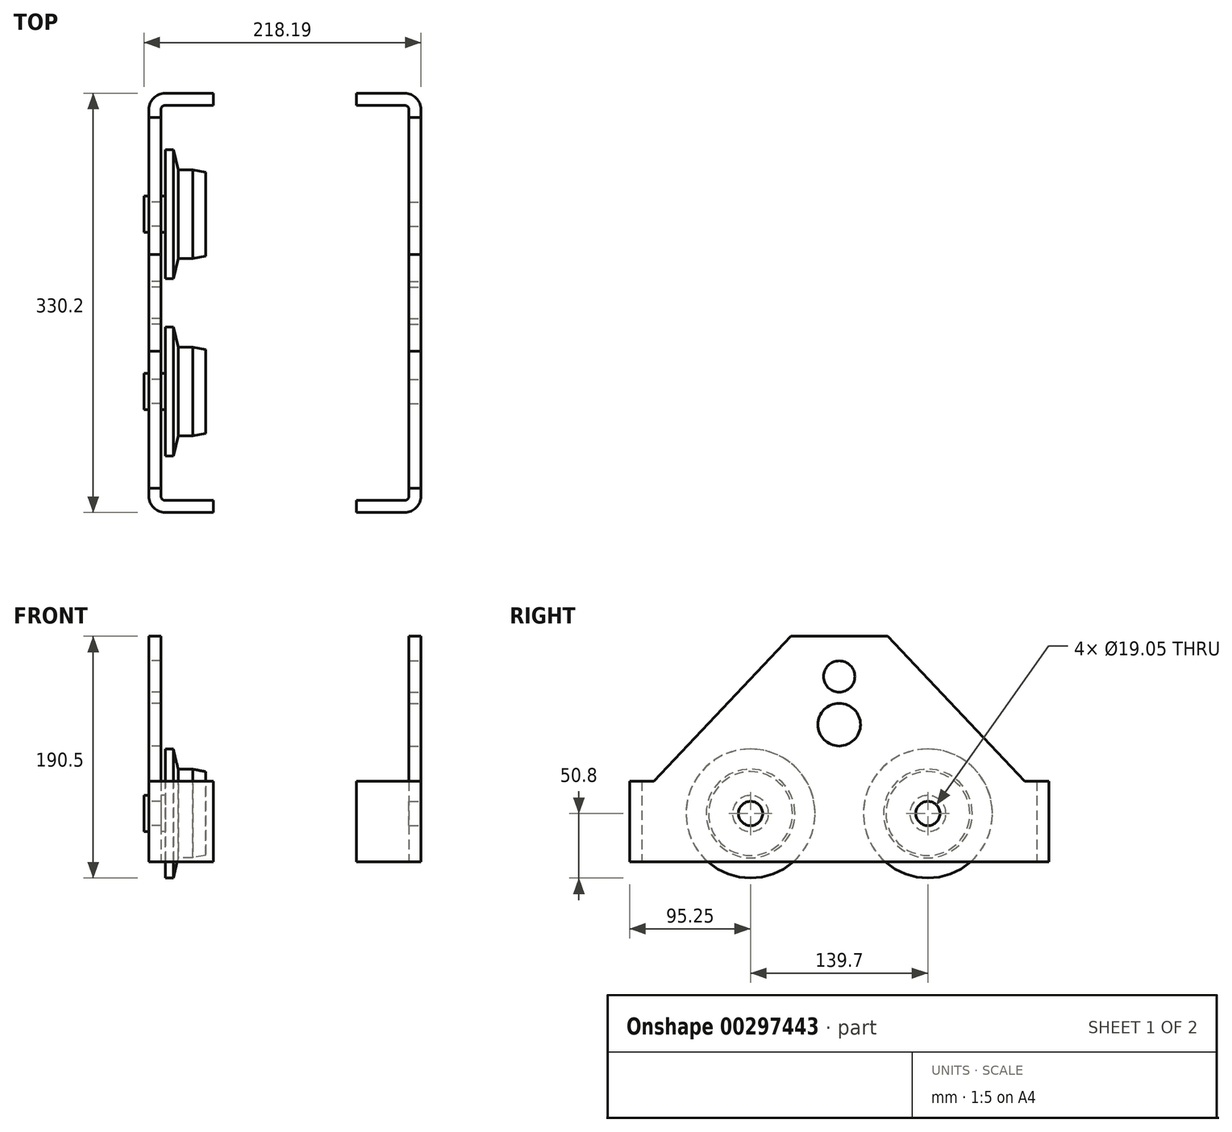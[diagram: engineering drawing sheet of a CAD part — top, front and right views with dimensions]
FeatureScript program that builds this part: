
annotation { "Feature Type Name" : "Feature", "Feature Type Description" : "" }
export const myFeature = defineFeature(function(context is Context, id is Id, definition is map)
    precondition{}
    {
        {
            var Q0;
            Q0=qCreatedBy(makeId("Top.planeOp"),FACE);
            var sketch = newSketch(context, id + "F0", { "sketchPlane" : qUnion([Q0])});
            skLineSegment(sketch, "E0", {"start": v(0, 0) * mm, "end": v(41.32, 0) * mm, "construction": true});
            skLineSegment(sketch, "E1", {"start": v(0, 0) * mm, "end": v(0, 152.4) * mm});
            skLineSegment(sketch, "E2", {"start": v(12.7, 165.1) * mm, "end": v(50.8, 165.1) * mm});
            skPoint(sketch, "E3.visualSharp", {"position": v(0, 165.1) * mm});
            skArc(sketch, "E3.filletArc", {"start": v(12.7, 165.1) * mm, "mid": v(3.72, 161.38) * mm, "end": v(0, 152.4) * mm});
            skLineSegment(sketch, "E4.MirrorCS", {"start": v(12.7, -165.1) * mm, "end": v(50.8, -165.1) * mm});
            skLineSegment(sketch, "E5.MirrorCS", {"start": v(0, 0) * mm, "end": v(0, -152.4) * mm});
            skArc(sketch, "E6.MirrorCS", {"start": v(12.7, -165.1) * mm, "mid": v(3.72, -161.38) * mm, "end": v(0, -152.4) * mm});
            skPoint(sketch, "E7.MirrorP", {"position": v(0, -165.1) * mm});
            skLineSegment(sketch, "E8.0", {"start": v(12.7, -155.58) * mm, "end": v(50.8, -155.58) * mm});
            skArc(sketch, "E8.1", {"start": v(12.7, -155.58) * mm, "mid": v(10.45, -154.65) * mm, "end": v(9.53, -152.4) * mm});
            skLineSegment(sketch, "E8.2", {"start": v(12.7, 155.58) * mm, "end": v(50.8, 155.58) * mm});
            skArc(sketch, "E8.3", {"start": v(12.7, 155.58) * mm, "mid": v(10.45, 154.65) * mm, "end": v(9.53, 152.4) * mm});
            skLineSegment(sketch, "E8.4", {"start": v(9.53, 0) * mm, "end": v(9.53, 152.4) * mm});
            skLineSegment(sketch, "E8.5", {"start": v(9.53, 0) * mm, "end": v(9.53, -152.4) * mm});
            skLineSegment(sketch, "E9", {"start": v(50.8, 165.1) * mm, "end": v(50.8, 155.58) * mm});
            skLineSegment(sketch, "E10", {"start": v(50.8, -155.58) * mm, "end": v(50.8, -165.1) * mm});
            skSolve(sketch);
        }
        {
            var Q0;
            Q0 = qSketchRegion(id + "F0", true);
            extrude(context, id + "F1", {"entities" : qUnion([Q0]), "depth" : 177.8 * mm});
        }
        {
            var Q0;
            Q0=makeQuery(id+"F1.opExtrude","SWEPT_FACE",FACE,{"disambiguationData":[OSD([sQuery(id+"F0.wireOp",EDGE,"E1"),sQuery(id+"F0.wireOp",EDGE,"E5.MirrorCS")])]});
            var sketch = newSketch(context, id + "F2", { "sketchPlane" : qUnion([Q0])});
            skLineSegment(sketch, "E11", {"start": v(-165.1, 63.5) * mm, "end": v(-146.05, 63.5) * mm});
            skLineSegment(sketch, "E12", {"start": v(-146.05, 63.5) * mm, "end": v(-38.1, 177.8) * mm});
            skLineSegment(sketch, "E13", {"start": v(-38.1, 177.8) * mm, "end": v(-165.1, 177.8) * mm});
            skPoint(sketch, "E13.endSnap0", {"position": v(0, 177.8) * mm});
            skLineSegment(sketch, "E14", {"start": v(-165.1, 177.8) * mm, "end": v(-165.1, 63.5) * mm});
            skLineSegment(sketch, "E15", {"start": v(0, 0) * mm, "end": v(0, 177.8) * mm, "construction": true});
            skCircle(sketch, "E16", {"center": v(-69.85, 38.1) * mm, "radius": 9.53 * mm});
            skLineSegment(sketch, "E17.MirrorCS", {"start": v(146.05, 63.5) * mm, "end": v(38.1, 177.8) * mm});
            skLineSegment(sketch, "E18.MirrorCS", {"start": v(38.1, 177.8) * mm, "end": v(165.1, 177.8) * mm});
            skLineSegment(sketch, "E19.MirrorCS", {"start": v(165.1, 177.8) * mm, "end": v(165.1, 63.5) * mm});
            skLineSegment(sketch, "E20.MirrorCS", {"start": v(165.1, 63.5) * mm, "end": v(146.05, 63.5) * mm});
            skCircle(sketch, "E21.MirrorC", {"center": v(69.85, 38.1) * mm, "radius": 9.53 * mm});
            skCircle(sketch, "E22", {"center": v(0, 108.08) * mm, "radius": 16.76 * mm});
            skCircle(sketch, "E23", {"center": v(0, 146.05) * mm, "radius": 12.32 * mm});
            skCircle(sketch, "E24", {"center": v(69.85, 38.1) * mm, "radius": 34.93 * mm, "construction": true});
            skCircle(sketch, "E25", {"center": v(-69.85, 38.1) * mm, "radius": 34.93 * mm, "construction": true});
            skLineSegment(sketch, "E26.bottom", {"start": v(-69.85, 73.02) * mm, "end": v(69.85, 73.02) * mm, "construction": true});
            skLineSegment(sketch, "E26.top", {"start": v(-69.85, 82.68) * mm, "end": v(69.85, 82.68) * mm, "construction": true});
            skLineSegment(sketch, "E26.left", {"start": v(-69.85, 73.02) * mm, "end": v(-69.85, 82.68) * mm, "construction": true});
            skLineSegment(sketch, "E26.right", {"start": v(69.85, 73.03) * mm, "end": v(69.85, 82.68) * mm, "construction": true});
            skSolve(sketch);
        }
        {
            var Q0;
            Q0 = qSketchRegion(id + "F2", true);
            extrude(context, id + "F3", {"entities" : qUnion([Q0]), "operationType" : NewBodyOperationType.REMOVE, "oppositeDirection" : true, "depth" : 50.8 * mm});
        }
        {
            var Q0;
            Q0=qCreatedBy(makeId("Front.planeOp"),FACE);
            var Q1;
            Q1=sQuery(id+"F2.wireOp",VERTEX,"E21.MirrorC.center");
            cPlane(context, id + "F4", {"entities" : qUnion([Q0, Q1]), "cplaneType" : CPlaneType.PLANE_POINT, "offset" : 25.4 * mm, "width" : 152.4 * mm, "height" : 152.4 * mm});
        }
        {
            var Q0;
            Q0=qCreatedBy(id+"F4.planeOp",FACE);
            var sketch = newSketch(context, id + "F5", { "sketchPlane" : qUnion([Q0])});
            skLineSegment(sketch, "E27", {"start": v(0, 38.1) * mm, "end": v(89.22, 38.1) * mm, "construction": true});
            skLineSegment(sketch, "E28", {"start": v(0, 38.1) * mm, "end": v(-3.94, 38.1) * mm});
            skLineSegment(sketch, "E29", {"start": v(-3.94, 38.1) * mm, "end": v(-3.94, 52.32) * mm});
            skLineSegment(sketch, "E30", {"start": v(-3.94, 52.32) * mm, "end": v(0, 52.32) * mm});
            skLineSegment(sketch, "E31", {"start": v(0, 52.32) * mm, "end": v(0, 47.63) * mm});
            skLineSegment(sketch, "E32", {"start": v(0, 47.63) * mm, "end": v(9.53, 47.63) * mm});
            skLineSegment(sketch, "E33", {"start": v(9.53, 47.63) * mm, "end": v(9.53, 52.32) * mm});
            skLineSegment(sketch, "E34", {"start": v(9.53, 52.32) * mm, "end": v(12.83, 52.32) * mm});
            skLineSegment(sketch, "E35", {"start": v(12.83, 52.32) * mm, "end": v(12.83, 88.9) * mm});
            skLineSegment(sketch, "E36", {"start": v(12.83, 88.9) * mm, "end": v(19.18, 88.9) * mm});
            skLineSegment(sketch, "E37", {"start": v(19.18, 88.9) * mm, "end": v(22.99, 73.03) * mm});
            skLineSegment(sketch, "E38", {"start": v(22.99, 73.03) * mm, "end": v(34.42, 73.03) * mm});
            skLineSegment(sketch, "E39", {"start": v(34.42, 73.03) * mm, "end": v(44.58, 71.12) * mm});
            skLineSegment(sketch, "E40", {"start": v(44.58, 71.12) * mm, "end": v(44.58, 38.1) * mm});
            skLineSegment(sketch, "E41", {"start": v(44.58, 38.1) * mm, "end": v(0, 38.1) * mm});
            skLineSegment(sketch, "E42", {"start": v(0, 47.63) * mm, "end": v(0, 47.63) * mm});
            skLineSegment(sketch, "E43.0", {"start": v(9.53, 177.8) * mm, "end": v(0, 177.8) * mm, "construction": true});
            skSolve(sketch);
        }
        {
            var Q0;
            Q0 = qSketchRegion(id + "F5", true);
            var Q1;
            Q1=sQuery(id+"F5.wireOp",EDGE,"E27");
            revolve(context, id + "F6", {"entities" : qUnion([Q0]), "axis" : qUnion([Q1]), "revolveType" : RevolveType.FULL});
        }
        {
            var Q0;
            Q0=makeQuery(id+"F6.opRevolve","SWEPT_BODY",BODY,{"disambiguationData":[OSD([sQuery(id+"F5.wireOp",EDGE,"E28"),sQuery(id+"F5.wireOp",EDGE,"E29"),sQuery(id+"F5.wireOp",EDGE,"E30"),sQuery(id+"F5.wireOp",EDGE,"E31"),sQuery(id+"F5.wireOp",EDGE,"E32"),sQuery(id+"F5.wireOp",EDGE,"E33"),sQuery(id+"F5.wireOp",EDGE,"E34"),sQuery(id+"F5.wireOp",EDGE,"E35"),sQuery(id+"F5.wireOp",EDGE,"E36"),sQuery(id+"F5.wireOp",EDGE,"E37"),sQuery(id+"F5.wireOp",EDGE,"E38"),sQuery(id+"F5.wireOp",EDGE,"E39"),sQuery(id+"F5.wireOp",EDGE,"E40"),sQuery(id+"F5.wireOp",EDGE,"E41")])]});
            var Q1;
            Q1=sQuery(id+"F2.wireOp",VERTEX,"E21.MirrorC.center");
            var Q2;
            Q2=sQuery(id+"F2.wireOp",VERTEX,"E16.center");
            transform(context, id + "F7", {"entities" : qUnion([Q0]), "transformType" : TransformType.TRANSLATION_ENTITY, "oppositeDirectionEntity" : false, "transformLine" : qUnion([Q1, Q2]), "makeCopy" : true});
        }
        {
            var Q0;
            Q0=qCreatedBy(makeId("Front.planeOp"),FACE);
            var sketch = newSketch(context, id + "F8", { "sketchPlane" : qUnion([Q0])});
            skLineSegment(sketch, "E44", {"start": v(22.99, 73.03) * mm, "end": v(107.12, 73.03) * mm, "construction": true});
            skLineSegment(sketch, "E45", {"start": v(107.12, 73.03) * mm, "end": v(107.12, 108.08) * mm, "construction": true});
            skLineSegment(sketch, "E46", {"start": v(107.12, 108.08) * mm, "end": v(9.52, 108.08) * mm, "construction": true});
            skLineSegment(sketch, "E47.0", {"start": v(9.52, 124.84) * mm, "end": v(9.52, 91.31) * mm, "construction": true});
            skSolve(sketch);
        }
        {
            var Q0;
            Q0=makeQuery(id+"F1.opExtrude","SWEPT_FACE",FACE,{"disambiguationData":[OSD([sQuery(id+"F0.wireOp",EDGE,"E1"),sQuery(id+"F0.wireOp",EDGE,"E5.MirrorCS")])]});
            var sketch = newSketch(context, id + "F9", { "sketchPlane" : qUnion([Q0])});
            skCircle(sketch, "E48", {"center": v(0, 146.05) * mm, "radius": 16.76 * mm});
            skSolve(sketch);
        }
        {
            var Q0;
            Q0=makeQuery(id+"F1.opExtrude","SWEPT_BODY",BODY,{"disambiguationData":[OSD([sQuery(id+"F0.wireOp",EDGE,"E1"),sQuery(id+"F0.wireOp",EDGE,"E2"),sQuery(id+"F0.wireOp",EDGE,"E3.filletArc"),sQuery(id+"F0.wireOp",EDGE,"E4.MirrorCS"),sQuery(id+"F0.wireOp",EDGE,"E5.MirrorCS"),sQuery(id+"F0.wireOp",EDGE,"E6.MirrorCS"),sQuery(id+"F0.wireOp",EDGE,"E8.0"),sQuery(id+"F0.wireOp",EDGE,"E8.1"),sQuery(id+"F0.wireOp",EDGE,"E8.2"),sQuery(id+"F0.wireOp",EDGE,"E8.3"),sQuery(id+"F0.wireOp",EDGE,"E8.4"),sQuery(id+"F0.wireOp",EDGE,"E8.5"),sQuery(id+"F0.wireOp",EDGE,"E9"),sQuery(id+"F0.wireOp",EDGE,"E10")])]});
            var Q1;
            Q1=sQuery(id+"F8.wireOp",EDGE,"E45");
            transform(context, id + "F10", {"entities" : qUnion([Q0]), "transformType" : TransformType.ROTATION, "transformAxis" : qUnion([Q1]), "angle" : 180 * degree, "makeCopy" : true});
        }
    });
